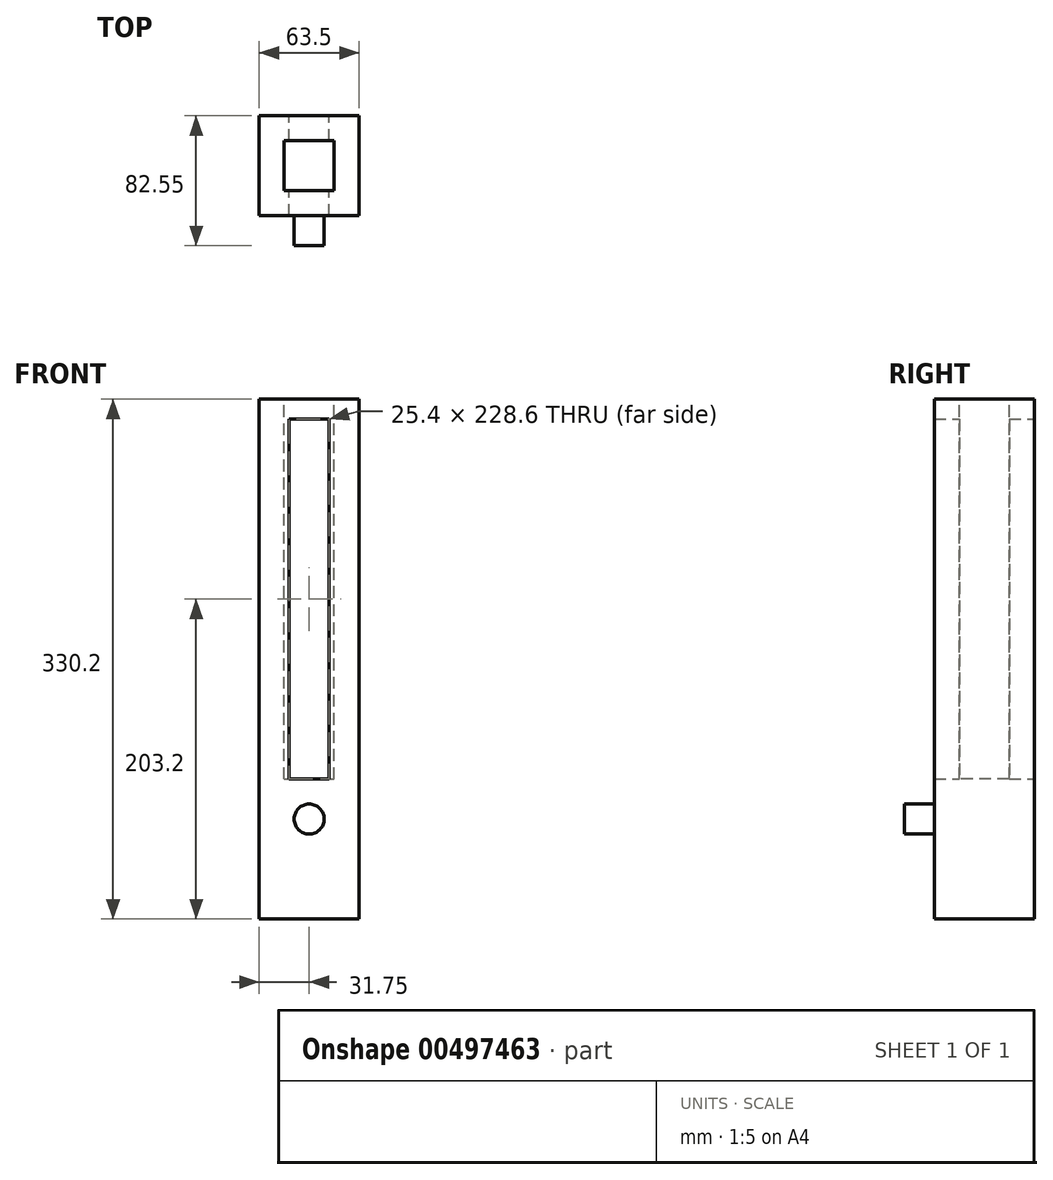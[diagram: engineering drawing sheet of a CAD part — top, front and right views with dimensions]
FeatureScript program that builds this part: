
annotation { "Feature Type Name" : "Feature", "Feature Type Description" : "" }
export const myFeature = defineFeature(function(context is Context, id is Id, definition is map)
    precondition{}
    {
        {
            var Q0;
            Q0=qCreatedBy(makeId("Front.planeOp"),FACE);
            var sketch = newSketch(context, id + "F0", { "sketchPlane" : qUnion([Q0])});
            skLineSegment(sketch, "E0.bottom", {"start": v(31.75, 165.1) * mm, "end": v(-31.75, 165.1) * mm});
            skLineSegment(sketch, "E0.top", {"start": v(31.75, -165.1) * mm, "end": v(-31.75, -165.1) * mm});
            skLineSegment(sketch, "E0.left", {"start": v(31.75, 165.1) * mm, "end": v(31.75, -165.1) * mm});
            skLineSegment(sketch, "E0.right", {"start": v(-31.75, 165.1) * mm, "end": v(-31.75, -165.1) * mm});
            skPoint(sketch, "E0.middle", {"position": v(0, 0) * mm});
            skLineSegment(sketch, "E1.bottom", {"start": v(-12.7, 152.4) * mm, "end": v(12.7, 152.4) * mm});
            skLineSegment(sketch, "E1.top", {"start": v(-12.7, -76.2) * mm, "end": v(12.7, -76.2) * mm});
            skLineSegment(sketch, "E1.left", {"start": v(-12.7, 152.4) * mm, "end": v(-12.7, -76.2) * mm});
            skLineSegment(sketch, "E1.right", {"start": v(12.7, 152.4) * mm, "end": v(12.7, -76.2) * mm});
            skSolve(sketch);
        }
        {
            var Q0;
            Q0=makeQuery(id+"F0.imprint","IMPRINT",FACE,{"disambiguationData":[TD([[makeQuery(id+"F0.imprint","IMPRINT",EDGE,{"derivedFrom":sQuery(id+"F0.wireOp",EDGE,"E0.bottom")}),1.0]])]});
            extrude(context, id + "F1", {"entities" : qUnion([Q0]), "endBound" : BoundingType.SYMMETRIC, "depth" : 63.5 * mm});
        }
        {
            var Q0;
            Q0=makeQuery(id+"F1.opExtrude","SWEPT_FACE",FACE,{"disambiguationData":[OSD([sQuery(id+"F0.wireOp",EDGE,"E0.bottom")])]});
            var sketch = newSketch(context, id + "F2", { "sketchPlane" : qUnion([Q0])});
            skLineSegment(sketch, "E2.bottom", {"start": v(-15.87, 15.88) * mm, "end": v(15.88, 15.88) * mm});
            skLineSegment(sketch, "E2.top", {"start": v(-15.88, -15.88) * mm, "end": v(15.87, -15.88) * mm});
            skLineSegment(sketch, "E2.left", {"start": v(-15.87, 15.88) * mm, "end": v(-15.88, -15.87) * mm});
            skLineSegment(sketch, "E2.right", {"start": v(15.88, 15.88) * mm, "end": v(15.87, -15.87) * mm});
            skPoint(sketch, "E2.middle", {"position": v(0, 0) * mm});
            skSolve(sketch);
        }
        {
            var Q0;
            Q0=makeQuery(id+"F2.imprint","IMPRINT",FACE,{"disambiguationData":[TD([[makeQuery(id+"F2.imprint","IMPRINT",EDGE,{"derivedFrom":sQuery(id+"F2.wireOp",EDGE,"E2.bottom")}),-1.0]])]});
            extrude(context, id + "F3", {"entities" : qUnion([Q0]), "operationType" : NewBodyOperationType.REMOVE, "oppositeDirection" : true, "depth" : 241.3 * mm});
        }
        {
            var Q0;
            Q0=makeQuery(id+"F1.opExtrude","CAP_FACE",FACE,{"disambiguationData":[OSD([sQuery(id+"F0.wireOp",EDGE,"E0.bottom"),sQuery(id+"F0.wireOp",EDGE,"E0.top"),sQuery(id+"F0.wireOp",EDGE,"E0.left"),sQuery(id+"F0.wireOp",EDGE,"E0.right"),sQuery(id+"F0.wireOp",EDGE,"E1.bottom"),sQuery(id+"F0.wireOp",EDGE,"E1.top"),sQuery(id+"F0.wireOp",EDGE,"E1.left"),sQuery(id+"F0.wireOp",EDGE,"E1.right")])],"isStart":false});
            var sketch = newSketch(context, id + "F4", { "sketchPlane" : qUnion([Q0])});
            skCircle(sketch, "E3", {"center": v(0, -101.6) * mm, "radius": 9.53 * mm});
            skPoint(sketch, "E3.centerSnap0", {"position": v(0, -76.2) * mm});
            skSolve(sketch);
        }
        {
            var Q0;
            Q0=makeQuery(id+"F4.imprint","IMPRINT",FACE,{"disambiguationData":[TD([[makeQuery(id+"F4.imprint","IMPRINT",EDGE,{"derivedFrom":sQuery(id+"F4.wireOp",EDGE,"E3")}),1.0]])]});
            extrude(context, id + "F5", {"entities" : qUnion([Q0]), "operationType" : NewBodyOperationType.ADD, "depth" : 19.05 * mm});
        }
    });
